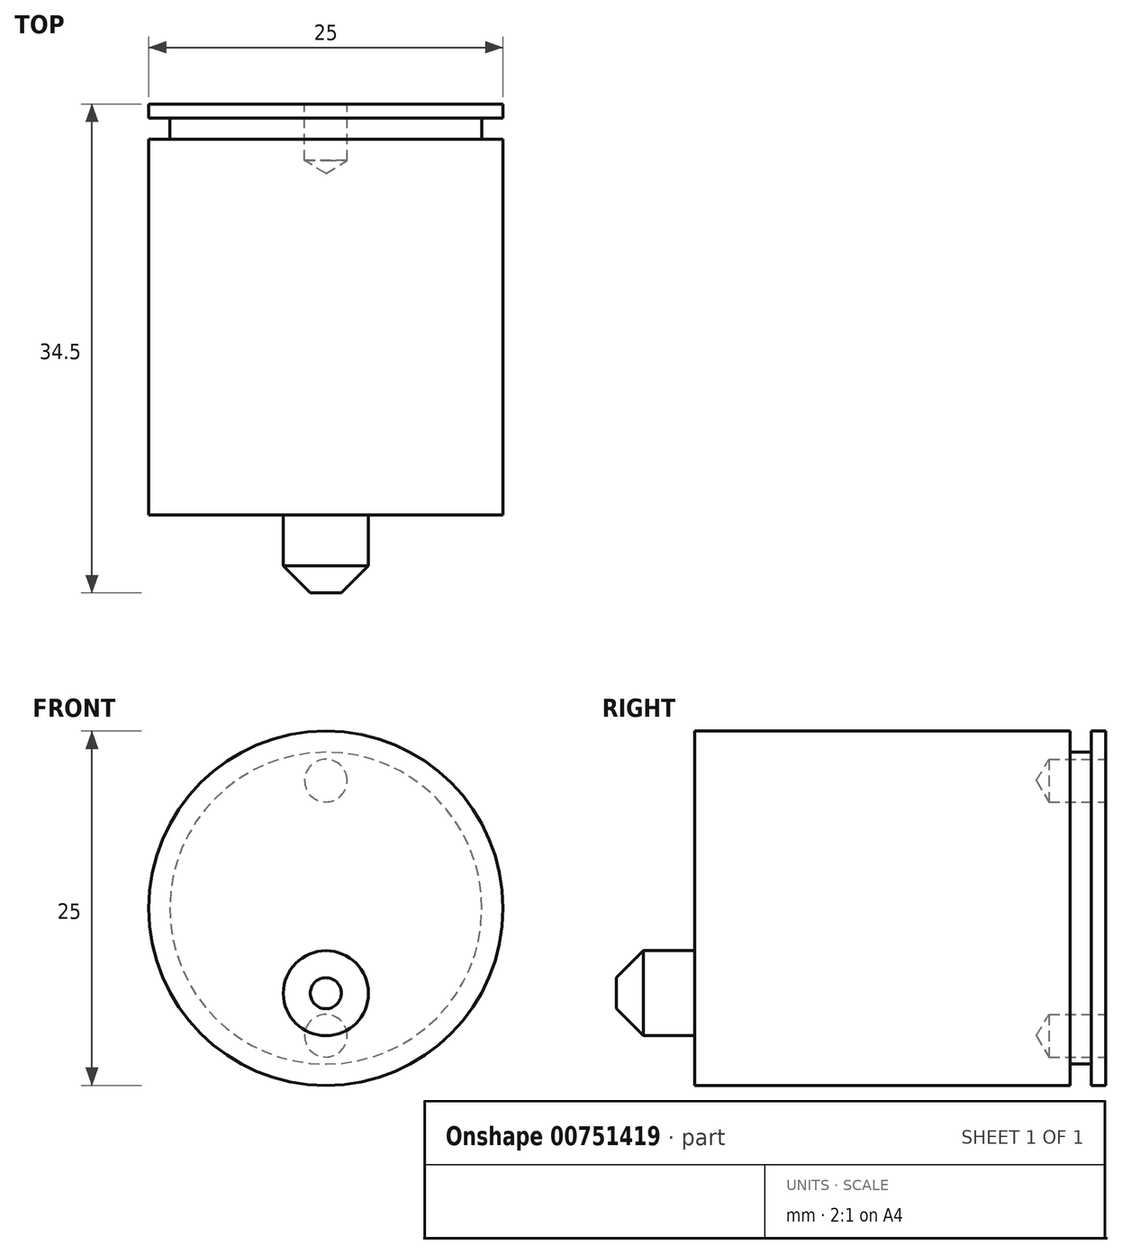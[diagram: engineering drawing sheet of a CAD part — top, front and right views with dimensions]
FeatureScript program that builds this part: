
annotation { "Feature Type Name" : "Feature", "Feature Type Description" : "" }
export const myFeature = defineFeature(function(context is Context, id is Id, definition is map)
    precondition{}
    {
        {
            var Q0;
            Q0=qCreatedBy(makeId("Top.planeOp"),FACE);
            var sketch = newSketch(context, id + "F0", { "sketchPlane" : qUnion([Q0])});
            skLineSegment(sketch, "E0", {"start": v(0, 47.03) * mm, "end": v(0, -40.17) * mm, "construction": true});
            skLineSegment(sketch, "E1.bottom", {"start": v(0, 29) * mm, "end": v(12.5, 29) * mm});
            skLineSegment(sketch, "E1.top", {"start": v(0, 0) * mm, "end": v(12.5, 0) * mm});
            skLineSegment(sketch, "E1.left", {"start": v(0, 29) * mm, "end": v(0, 0) * mm});
            skLineSegment(sketch, "E1.right", {"start": v(12.5, 29) * mm, "end": v(12.5, 28) * mm});
            skLineSegment(sketch, "E2.bottom", {"start": v(6, 29) * mm, "end": v(0, 29) * mm});
            skLineSegment(sketch, "E2.top", {"start": v(6, 31) * mm, "end": v(0, 31) * mm});
            skLineSegment(sketch, "E2.left", {"start": v(6, 29) * mm, "end": v(6, 31) * mm});
            skLineSegment(sketch, "E2.right", {"start": v(0, 29) * mm, "end": v(0, 31) * mm});
            skLineSegment(sketch, "E3.bottom", {"start": v(2, 31) * mm, "end": v(0, 31) * mm});
            skLineSegment(sketch, "E3.top", {"start": v(2, 41) * mm, "end": v(0, 41) * mm});
            skLineSegment(sketch, "E3.left", {"start": v(2, 31) * mm, "end": v(2, 41) * mm});
            skLineSegment(sketch, "E3.right", {"start": v(0, 31) * mm, "end": v(0, 41) * mm});
            skLineSegment(sketch, "E4.bottom", {"start": v(12.5, 28) * mm, "end": v(11, 28) * mm});
            skLineSegment(sketch, "E4.top", {"start": v(12.5, 26.5) * mm, "end": v(11, 26.5) * mm});
            skLineSegment(sketch, "E4.right", {"start": v(11, 28) * mm, "end": v(11, 26.5) * mm});
            skLineSegment(sketch, "E5.trimOffspring", {"start": v(12.5, 26.5) * mm, "end": v(12.5, 0) * mm});
            skSolve(sketch);
        }
        {
            var Q0;
            Q0=makeQuery(id+"F0.imprint","IMPRINT",FACE,{"disambiguationData":[TD([[makeQuery(id+"F0.imprint","IMPRINT",EDGE,{"derivedFrom":sQuery(id+"F0.wireOp",EDGE,"E1.bottom")}),-1.0]])]});
            var Q1;
            Q1=makeQuery(id+"F0.imprint","IMPRINT",FACE,{"disambiguationData":[TD([[makeQuery(id+"F0.imprint","IMPRINT",EDGE,{"derivedFrom":sQuery(id+"F0.wireOp",EDGE,"E2.bottom")}),-1.0]])]});
            var Q2;
            Q2=makeQuery(id+"F0.imprint","IMPRINT",FACE,{"disambiguationData":[TD([[makeQuery(id+"F0.imprint","IMPRINT",EDGE,{"derivedFrom":sQuery(id+"F0.wireOp",EDGE,"E3.bottom")}),-1.0]])]});
            var Q3;
            Q3=sQuery(id+"F0.wireOp",EDGE,"E1.left");
            revolve(context, id + "F1", {"surfaceOperationType" : NewSurfaceOperationType.NEW, "entities" : qUnion([Q0, Q1, Q2]), "axis" : qUnion([Q3]), "revolveType" : RevolveType.FULL});
        }
        {
            var Q0;
            Q0=makeQuery(id+"F1.opRevolve","SWEPT_FACE",FACE,{"disambiguationData":[OSD([sQuery(id+"F0.wireOp",EDGE,"E1.bottom")])]});
            var sketch = newSketch(context, id + "F2", { "sketchPlane" : qUnion([Q0])});
            skCircle(sketch, "E6", {"center": v(0, 0) * mm, "radius": 9 * mm, "construction": true});
            skPoint(sketch, "E7", {"position": v(0, 9) * mm});
            skPoint(sketch, "E8", {"position": v(0, -9) * mm});
            skSolve(sketch);
        }
        {
            var Q0;
            Q0=sQuery(id+"F2.wireOp",VERTEX,"E7");
            var Q1;
            Q1=sQuery(id+"F2.wireOp",VERTEX,"E8");
            var Q2;
            Q2=makeQuery(id+"F1.opRevolve","SWEPT_BODY",BODY,{"disambiguationData":[OSD([sQuery(id+"F0.wireOp",EDGE,"E1.bottom"),sQuery(id+"F0.wireOp",EDGE,"E1.top"),sQuery(id+"F0.wireOp",EDGE,"E1.left"),sQuery(id+"F0.wireOp",EDGE,"E1.right"),sQuery(id+"F0.wireOp",EDGE,"E2.top"),sQuery(id+"F0.wireOp",EDGE,"E2.left"),sQuery(id+"F0.wireOp",EDGE,"E2.right"),sQuery(id+"F0.wireOp",EDGE,"E3.top"),sQuery(id+"F0.wireOp",EDGE,"E3.left"),sQuery(id+"F0.wireOp",EDGE,"E3.right"),sQuery(id+"F0.wireOp",EDGE,"E4.bottom"),sQuery(id+"F0.wireOp",EDGE,"E4.top"),sQuery(id+"F0.wireOp",EDGE,"E4.right"),sQuery(id+"F0.wireOp",EDGE,"E5.trimOffspring")])]});
            hole(context, id + "F3", {"style" : HoleStyle.SIMPLE, "endStyle" : HoleEndStyle.BLIND, "standardTappedOrClearance" : lookupTablePath({ "standard" : "ISO", "size" : "3", "type" : "Drilled" }), "standardBlindInLast" : lookupTablePath({ "standard" : "ISO", "size" : "3", "type" : "Drilled" }), "holeDiameter" : 3 * mm, "majorDiameter" : 6.35 * mm, "holeDepth" : 4 * mm, "isTappedThrough" : true, "tappedDepth" : 12.7 * mm, "tapClearance" : 3, "locations" : qUnion([Q0, Q1]), "scope" : qUnion([Q2])});
        }
        {
            var Q0;
            Q0=makeQuery(id+"F1.opRevolve","SWEPT_FACE",FACE,{"disambiguationData":[OSD([sQuery(id+"F0.wireOp",EDGE,"E1.top")])]});
            var sketch = newSketch(context, id + "F4", { "sketchPlane" : qUnion([Q0])});
            skCircle(sketch, "E9", {"center": v(0, -6) * mm, "radius": 3 * mm});
            skSolve(sketch);
        }
        {
            var Q0;
            Q0=makeQuery(id+"F4.imprint","IMPRINT",FACE,{"disambiguationData":[TD([[makeQuery(id+"F4.imprint","IMPRINT",EDGE,{"derivedFrom":sQuery(id+"F4.wireOp",EDGE,"E9")}),1.0]])]});
            extrude(context, id + "F5", {"entities" : qUnion([Q0]), "operationType" : NewBodyOperationType.ADD, "depth" : 5.5 * mm, "offsetDistance" : 25.4 * mm});
        }
        {
            var Q0;
            Q0=makeQuery(id+"F5.opExtrude","CAP_EDGE",EDGE,{"disambiguationData":[OSD([sQuery(id+"F4.wireOp",EDGE,"E9")])],"isStart":false});
            chamfer(context, id + "F6", {"entities" : qUnion([Q0]), "width" : 1.9 * mm, "tangentPropagation" : true});
        }
    });
